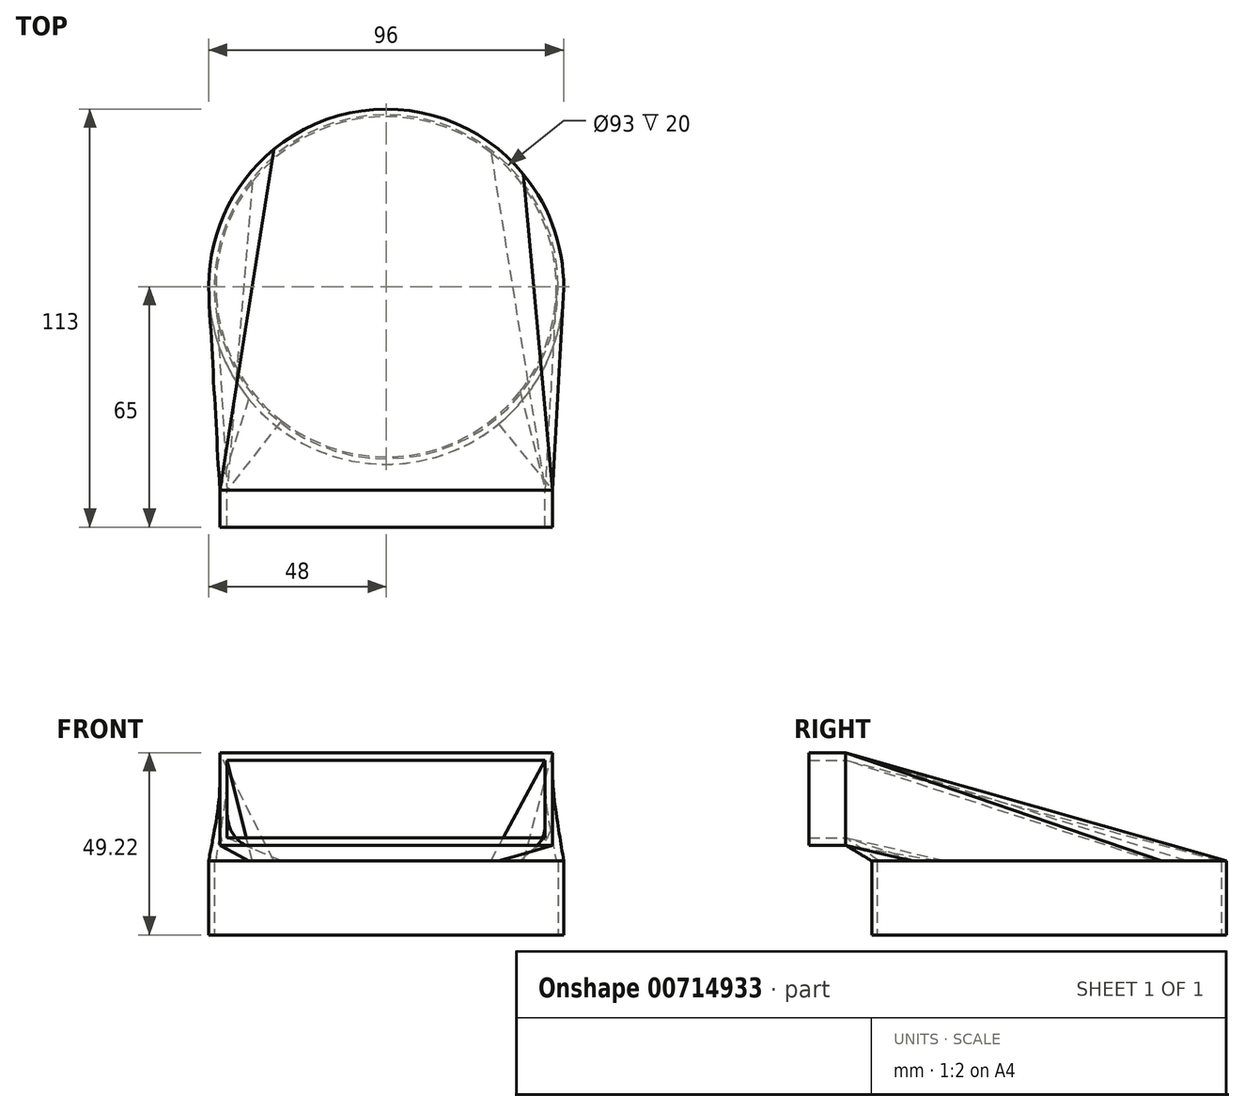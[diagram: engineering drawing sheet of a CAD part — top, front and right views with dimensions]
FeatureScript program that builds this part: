
annotation { "Feature Type Name" : "Feature", "Feature Type Description" : "" }
export const myFeature = defineFeature(function(context is Context, id is Id, definition is map)
    precondition{}
    {
        {
            var Q0;
            Q0=qCreatedBy(makeId("Top.planeOp"),FACE);
            var sketch = newSketch(context, id + "F0", { "sketchPlane" : qUnion([Q0])});
            skCircle(sketch, "E0.0", {"center": v(0, 0) * mm, "radius": 48 * mm});
            skSolve(sketch);
        }
        {
            var Q0;
            Q0 = qSketchRegion(id + "F0", true);
            extrude(context, id + "F1", {"entities" : qUnion([Q0]), "depth" : 20 * mm, "offsetDistance" : 25 * mm});
        }
        {
            var Q0;
            Q0=qCreatedBy(makeId("Front.planeOp"),FACE);
            cPlane(context, id + "F2", {"entities" : qUnion([Q0]), "cplaneType" : CPlaneType.OFFSET, "offset" : 55 * mm, "width" : 150 * mm, "height" : 150 * mm});
        }
        {
            var Q0;
            Q0=qCreatedBy(id+"F2.planeOp",FACE);
            var sketch = newSketch(context, id + "F3", { "sketchPlane" : qUnion([Q0])});
            skLineSegment(sketch, "E1.bottom", {"start": v(45, 49.22) * mm, "end": v(-45, 49.22) * mm});
            skLineSegment(sketch, "E1.top", {"start": v(45, 24.22) * mm, "end": v(-45, 24.22) * mm});
            skLineSegment(sketch, "E1.left", {"start": v(45, 49.22) * mm, "end": v(45, 24.22) * mm});
            skLineSegment(sketch, "E1.right", {"start": v(-45, 49.22) * mm, "end": v(-45, 24.22) * mm});
            skPoint(sketch, "E1.middle", {"position": v(0, 36.72) * mm});
            skSolve(sketch);
        }
        {
            var Q0;
            Q0 = qSketchRegion(id + "F3", true);
            extrude(context, id + "F4", {"entities" : qUnion([Q0]), "depth" : 10 * mm, "offsetDistance" : 25 * mm});
        }
        {
            var Q1;
            Q1=makeQuery(id+"F1.opExtrude","CAP_FACE",FACE,{"disambiguationData":[OSD([sQuery(id+"F0.wireOp",EDGE,"E0.0")])],"isStart":false});
            var Q2;
            Q2=makeQuery(id+"F4.opExtrude","CAP_FACE",FACE,{"disambiguationData":[OSD([sQuery(id+"F3.wireOp",EDGE,"E1.bottom"),sQuery(id+"F3.wireOp",EDGE,"E1.top"),sQuery(id+"F3.wireOp",EDGE,"E1.left"),sQuery(id+"F3.wireOp",EDGE,"E1.right")])],"isStart":true});
            loft(context, id + "F5", {"operationType" : NewBodyOperationType.ADD, "sheetProfilesArray" : [{ "sheetProfileEntities" : qUnion([Q1]) }, { "sheetProfileEntities" : qUnion([Q2]) }]});
        }
        {
            var Q0;
            Q0=qCreatedBy(id+"F2.planeOp",FACE);
            var sketch = newSketch(context, id + "F6", { "sketchPlane" : qUnion([Q0])});
            skLineSegment(sketch, "E2.0", {"start": v(-43, 26.22) * mm, "end": v(43, 26.22) * mm});
            skLineSegment(sketch, "E2.1", {"start": v(-43, 47.22) * mm, "end": v(-43, 26.22) * mm});
            skLineSegment(sketch, "E2.2", {"start": v(43, 47.22) * mm, "end": v(-43, 47.22) * mm});
            skLineSegment(sketch, "E2.3", {"start": v(43, 26.22) * mm, "end": v(43, 47.22) * mm});
            skSolve(sketch);
        }
        {
            var Q0;
            Q0=qCreatedBy(makeId("Top.planeOp"),FACE);
            var sketch = newSketch(context, id + "F7", { "sketchPlane" : qUnion([Q0])});
            skCircle(sketch, "E3.0", {"center": v(0, 0) * mm, "radius": 46.5 * mm});
            skSolve(sketch);
        }
        {
            var Q0;
            Q0=qCreatedBy(makeId("Top.planeOp"),FACE);
            cPlane(context, id + "F8", {"entities" : qUnion([Q0]), "cplaneType" : CPlaneType.OFFSET, "offset" : 20 * mm, "width" : 150 * mm, "height" : 150 * mm});
        }
        {
            var Q0;
            Q0=qCreatedBy(id+"F8.planeOp",FACE);
            var sketch = newSketch(context, id + "F9", { "sketchPlane" : qUnion([Q0])});
            skCircle(sketch, "E4.0", {"center": v(0, 0) * mm, "radius": 46 * mm});
            skSolve(sketch);
        }
        {
            var Q0;
            Q0 = qSketchRegion(id + "F9", true);
            var Q1;
            Q1 = qSketchRegion(id + "F6", true);
            loft(context, id + "F10", {"operationType" : NewBodyOperationType.REMOVE, "sheetProfilesArray" : [{ "sheetProfileEntities" : qUnion([Q0]) }, { "sheetProfileEntities" : qUnion([Q1]) }]});
        }
        {
            var Q0;
            Q0 = qSketchRegion(id + "F6", true);
            extrude(context, id + "F11", {"entities" : qUnion([Q0]), "operationType" : NewBodyOperationType.REMOVE, "depth" : 25 * mm, "offsetDistance" : 25 * mm});
        }
        {
            var Q0;
            Q0=makeQuery(id+"F7.imprint","IMPRINT",FACE,{"disambiguationData":[TD([[makeQuery(id+"F7.imprint","IMPRINT",EDGE,{"derivedFrom":sQuery(id+"F7.wireOp",EDGE,"E3.0")}),1.0]])]});
            extrude(context, id + "F12", {"entities" : qUnion([Q0]), "operationType" : NewBodyOperationType.REMOVE, "depth" : 20 * mm, "offsetDistance" : 25 * mm});
        }
    });
